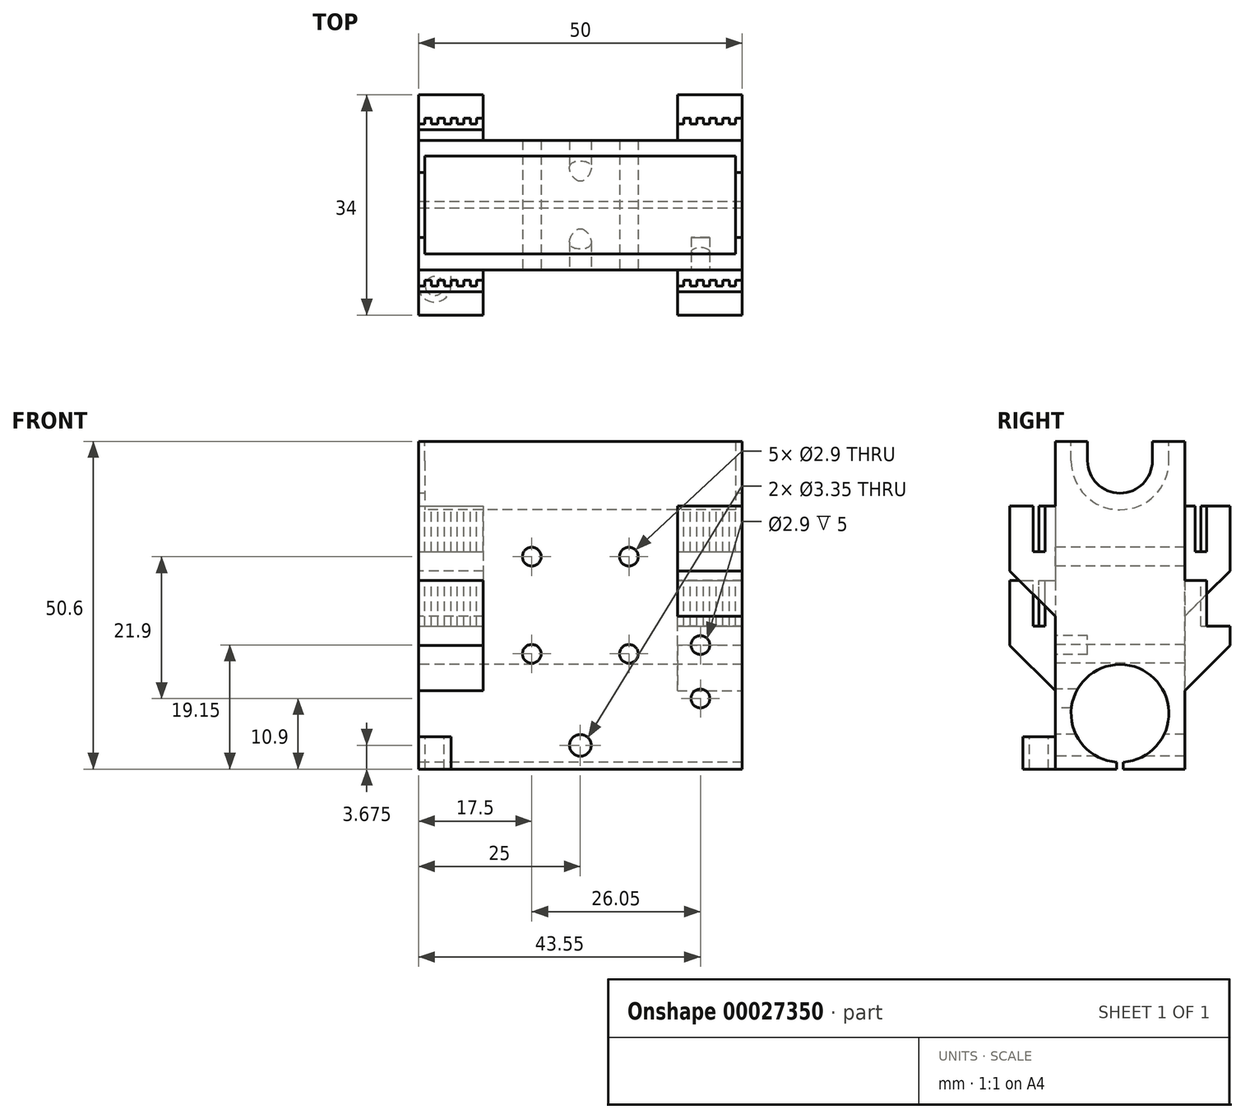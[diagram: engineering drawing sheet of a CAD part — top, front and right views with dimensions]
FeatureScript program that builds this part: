
annotation { "Feature Type Name" : "Feature", "Feature Type Description" : "" }
export const myFeature = defineFeature(function(context is Context, id is Id, definition is map)
    precondition{}
    {
        {
            var Q0;
            Q0=qCreatedBy(makeId("Top.planeOp"),FACE);
            var sketch = newSketch(context, id + "F0", { "sketchPlane" : qUnion([Q0])});
            skLineSegment(sketch, "E0.bottom", {"start": v(0, 0) * mm, "end": v(50, 0) * mm});
            skLineSegment(sketch, "E0.top", {"start": v(0, 20) * mm, "end": v(50, 20) * mm});
            skLineSegment(sketch, "E0.left", {"start": v(0, 0) * mm, "end": v(0, 20) * mm});
            skLineSegment(sketch, "E0.right", {"start": v(50, 0) * mm, "end": v(50, 20) * mm});
            skSolve(sketch);
        }
        {
            var Q0;
            Q0=qSketchRegion(id+"F0",true);
            extrude(context, id + "F1", {"entities" : qUnion([Q0]), "depth" : 50.6 * mm});
        }
        {
            var Q0;
            Q0=makeQuery(id+"F1.opExtrude","SWEPT_FACE",FACE,{"disambiguationData":[OSD([sQuery(id+"F0.wireOp",EDGE,"E0.left")])]});
            var sketch = newSketch(context, id + "F2", { "sketchPlane" : qUnion([Q0])});
            skCircle(sketch, "E1", {"center": v(-10, 8.6) * mm, "radius": 7.55 * mm});
            skCircle(sketch, "E2", {"center": v(-10, 47.6) * mm, "radius": 5 * mm});
            skLineSegment(sketch, "E3", {"start": v(-20, 47.6) * mm, "end": v(0, 47.6) * mm, "construction": true});
            skLineSegment(sketch, "E4", {"start": v(-15, 50.6) * mm, "end": v(-15, 47.6) * mm});
            skLineSegment(sketch, "E5", {"start": v(-5, 50.6) * mm, "end": v(-5, 47.6) * mm});
            skLineSegment(sketch, "E6", {"start": v(-20, 8.6) * mm, "end": v(0, 8.6) * mm, "construction": true});
            skLineSegment(sketch, "E7", {"start": v(-10, 8.6) * mm, "end": v(-10, 0) * mm, "construction": true});
            skLineSegment(sketch, "E8", {"start": v(-10, 0) * mm, "end": v(-10.5, 0) * mm});
            skLineSegment(sketch, "E9", {"start": v(-10.5, 0) * mm, "end": v(-10.5, 1.07) * mm});
            skLineSegment(sketch, "E10", {"start": v(-10.5, 1.07) * mm, "end": v(-9.5, 1.07) * mm});
            skLineSegment(sketch, "E11", {"start": v(-9.5, 1.07) * mm, "end": v(-9.5, 0) * mm});
            skLineSegment(sketch, "E12", {"start": v(-9.5, 0) * mm, "end": v(-10, 0) * mm});
            skLineSegment(sketch, "E13", {"start": v(-10, 15.6) * mm, "end": v(-10, 16.15) * mm});
            skLineSegment(sketch, "E14", {"start": v(-10, 15.6) * mm, "end": v(-5.53, 14.68) * mm});
            skLineSegment(sketch, "E15", {"start": v(-10, 15.6) * mm, "end": v(-14.47, 14.68) * mm});
            skCircle(sketch, "E16", {"center": v(-10, 47.6) * mm, "radius": 7.55 * mm});
            skLineSegment(sketch, "E17", {"start": v(-2.45, 47.6) * mm, "end": v(-2.45, 50.6) * mm});
            skLineSegment(sketch, "E18", {"start": v(-17.55, 47.6) * mm, "end": v(-17.55, 50.6) * mm});
            skSolve(sketch);
        }
        {
            var Q0;
            {var subQ0=sQuery(id+"F2.wireOp",EDGE,"E14");var subQ1=sQuery(id+"F2.wireOp",EDGE,"E1");var subQ3=makeQuery(id+"F2.imprint","INTERSECT",VERTEX,{"disambiguationData":[OD(0.0)],"derivedFrom":[subQ1,subQ0]});Q0=makeQuery(id+"F2.imprint","IMPRINT",FACE,{"disambiguationData":[TD([[makeQuery(id+"F2.imprint","IMPRINT",EDGE,{"disambiguationData":[TD([[subQ3,-1.0]])],"derivedFrom":subQ1}),1.0]])]});}
            var Q1;
            {var subQ0=sQuery(id+"F2.wireOp",EDGE,"E15");var subQ1=sQuery(id+"F2.wireOp",EDGE,"E1");var subQ3=makeQuery(id+"F2.imprint","INTERSECT",VERTEX,{"disambiguationData":[OD(0.0)],"derivedFrom":[subQ1,subQ0]});Q1=makeQuery(id+"F2.imprint","IMPRINT",FACE,{"disambiguationData":[TD([[makeQuery(id+"F2.imprint","IMPRINT",EDGE,{"disambiguationData":[TD([[subQ3,1.0]])],"derivedFrom":subQ1}),1.0]])]});}
            var Q2;
            Q2=makeQuery(id+"F2.imprint","IMPRINT",FACE,{"disambiguationData":[TD([[makeQuery(id+"F2.imprint","IMPRINT",EDGE,{"derivedFrom":sQuery(id+"F2.wireOp",EDGE,"E8")}),-1.0]])]});
            var Q3;
            {var subQ0=sQuery(id+"F2.wireOp",EDGE,"E10");Q3=makeQuery(id+"F2.imprint","IMPRINT",FACE,{"disambiguationData":[TD([[makeQuery(id+"F2.imprint","IMPRINT",EDGE,{"derivedFrom":subQ0}),-1.0]])]});}
            var Q4;
            {var subQ3=sQuery(id+"F2.wireOp",EDGE,"E13");Q4=makeQuery(id+"F2.imprint","IMPRINT",FACE,{"disambiguationData":[TD([[makeQuery(id+"F2.imprint","IMPRINT",EDGE,{"derivedFrom":subQ3}),-1.0]])]});}
            var Q5;
            {var subQ3=sQuery(id+"F2.wireOp",EDGE,"E13");Q5=makeQuery(id+"F2.imprint","IMPRINT",FACE,{"disambiguationData":[TD([[makeQuery(id+"F2.imprint","IMPRINT",EDGE,{"derivedFrom":subQ3}),1.0]])]});}
            var Q6;
            {var subQ7=sQuery(id+"F2.wireOp",EDGE,"E10");Q6=makeQuery(id+"F2.imprint","IMPRINT",FACE,{"disambiguationData":[TD([[makeQuery(id+"F2.imprint","IMPRINT",EDGE,{"derivedFrom":subQ7}),1.0]])]});}
            var Q7;
            {var subQ3=sQuery(id+"F2.wireOp",EDGE,"E5");Q7=makeQuery(id+"F2.imprint","IMPRINT",FACE,{"disambiguationData":[TD([[makeQuery(id+"F2.imprint","IMPRINT",EDGE,{"derivedFrom":subQ3}),-1.0]])]});}
            var Q8;
            {var subQ0=sQuery(id+"F2.wireOp",EDGE,"E4");Q8=makeQuery(id+"F2.imprint","IMPRINT",FACE,{"disambiguationData":[TD([[makeQuery(id+"F2.imprint","IMPRINT",EDGE,{"derivedFrom":subQ0}),1.0]])]});}
            var Q9;
            {var subQ0=sQuery(id+"F2.wireOp",EDGE,"E4");Q9=makeQuery(id+"F2.imprint","IMPRINT",FACE,{"disambiguationData":[TD([[makeQuery(id+"F2.imprint","IMPRINT",EDGE,{"derivedFrom":subQ0}),1.0]])]});}
            var Q10;
            {var subQ3=sQuery(id+"F2.wireOp",EDGE,"E5");Q10=makeQuery(id+"F2.imprint","IMPRINT",FACE,{"disambiguationData":[TD([[makeQuery(id+"F2.imprint","IMPRINT",EDGE,{"derivedFrom":subQ3}),-1.0]])]});}
            var Q11;
            {var subQ1=sQuery(id+"F2.wireOp",EDGE,"E2");var subQ4=makeQuery(id+"F2.imprint","INTERSECT",VERTEX,{"derivedFrom":[subQ1,sQuery(id+"F2.wireOp",EDGE,"E5")]});Q11=makeQuery(id+"F2.imprint","IMPRINT",FACE,{"disambiguationData":[TD([[makeQuery(id+"F2.imprint","IMPRINT",EDGE,{"disambiguationData":[TD([[subQ4,-1.0]])],"derivedFrom":subQ1}),1.0]])]});}
            extrude(context, id + "F3", {"entities" : qUnion([Q0, Q1, Q2, Q3, Q4, Q5, Q6, Q7, Q8, Q9, Q10, Q11]), "operationType" : NewBodyOperationType.REMOVE, "endBound" : BoundingType.THROUGH_ALL, "oppositeDirection" : true, "depth" : 25 * mm});
        }
        {
            var Q0;
            {var subQ3=sQuery(id+"F2.wireOp",EDGE,"E4");Q0=makeQuery(id+"F2.imprint","IMPRINT",FACE,{"disambiguationData":[TD([[makeQuery(id+"F2.imprint","IMPRINT",EDGE,{"derivedFrom":subQ3}),-1.0]])]});}
            var Q1;
            {var subQ3=sQuery(id+"F2.wireOp",EDGE,"E18");Q1=makeQuery(id+"F2.imprint","IMPRINT",FACE,{"disambiguationData":[TD([[makeQuery(id+"F2.imprint","IMPRINT",EDGE,{"derivedFrom":subQ3}),-1.0]])]});}
            var Q2;
            {var subQ3=sQuery(id+"F2.wireOp",EDGE,"E17");Q2=makeQuery(id+"F2.imprint","IMPRINT",FACE,{"disambiguationData":[TD([[makeQuery(id+"F2.imprint","IMPRINT",EDGE,{"derivedFrom":subQ3}),1.0]])]});}
            extrude(context, id + "F4", {"entities" : qUnion([Q0, Q1, Q2]), "operationType" : NewBodyOperationType.REMOVE, "oppositeDirection" : true, "depth" : 49 * mm});
        }
        {
            var Q0;
            {var subQ3=sQuery(id+"F2.wireOp",EDGE,"E4");Q0=makeQuery(id+"F2.imprint","IMPRINT",FACE,{"disambiguationData":[TD([[makeQuery(id+"F2.imprint","IMPRINT",EDGE,{"derivedFrom":subQ3}),-1.0]])]});}
            var Q1;
            {var subQ3=sQuery(id+"F2.wireOp",EDGE,"E18");Q1=makeQuery(id+"F2.imprint","IMPRINT",FACE,{"disambiguationData":[TD([[makeQuery(id+"F2.imprint","IMPRINT",EDGE,{"derivedFrom":subQ3}),-1.0]])]});}
            var Q2;
            {var subQ3=sQuery(id+"F2.wireOp",EDGE,"E17");Q2=makeQuery(id+"F2.imprint","IMPRINT",FACE,{"disambiguationData":[TD([[makeQuery(id+"F2.imprint","IMPRINT",EDGE,{"derivedFrom":subQ3}),1.0]])]});}
            extrude(context, id + "F5", {"entities" : qUnion([Q0, Q1, Q2]), "operationType" : NewBodyOperationType.ADD, "oppositeDirection" : true, "depth" : 16.21 * mm});
        }
        {
            var Q0;
            {var subQ3=sQuery(id+"F2.wireOp",EDGE,"E4");Q0=makeQuery(id+"F2.imprint","IMPRINT",FACE,{"disambiguationData":[TD([[makeQuery(id+"F2.imprint","IMPRINT",EDGE,{"derivedFrom":subQ3}),-1.0]])]});}
            var Q1;
            {var subQ3=sQuery(id+"F2.wireOp",EDGE,"E18");Q1=makeQuery(id+"F2.imprint","IMPRINT",FACE,{"disambiguationData":[TD([[makeQuery(id+"F2.imprint","IMPRINT",EDGE,{"derivedFrom":subQ3}),-1.0]])]});}
            var Q2;
            {var subQ3=sQuery(id+"F2.wireOp",EDGE,"E17");Q2=makeQuery(id+"F2.imprint","IMPRINT",FACE,{"disambiguationData":[TD([[makeQuery(id+"F2.imprint","IMPRINT",EDGE,{"derivedFrom":subQ3}),1.0]])]});}
            extrude(context, id + "F6", {"entities" : qUnion([Q0, Q1, Q2]), "operationType" : NewBodyOperationType.REMOVE, "oppositeDirection" : true, "depth" : 23.25 * mm});
        }
        {
            var Q0;
            {var subQ3=sQuery(id+"F2.wireOp",EDGE,"E4");Q0=makeQuery(id+"F2.imprint","IMPRINT",FACE,{"disambiguationData":[TD([[makeQuery(id+"F2.imprint","IMPRINT",EDGE,{"derivedFrom":subQ3}),-1.0]])]});}
            var Q1;
            {var subQ3=sQuery(id+"F2.wireOp",EDGE,"E18");Q1=makeQuery(id+"F2.imprint","IMPRINT",FACE,{"disambiguationData":[TD([[makeQuery(id+"F2.imprint","IMPRINT",EDGE,{"derivedFrom":subQ3}),-1.0]])]});}
            var Q2;
            {var subQ3=sQuery(id+"F2.wireOp",EDGE,"E17");Q2=makeQuery(id+"F2.imprint","IMPRINT",FACE,{"disambiguationData":[TD([[makeQuery(id+"F2.imprint","IMPRINT",EDGE,{"derivedFrom":subQ3}),1.0]])]});}
            extrude(context, id + "F7", {"entities" : qUnion([Q0, Q1, Q2]), "operationType" : NewBodyOperationType.ADD, "oppositeDirection" : true, "depth" : 1 * mm});
        }
        {
            var Q0;
            Q0=makeQuery(id+"F1.opExtrude","SWEPT_FACE",FACE,{"disambiguationData":[OSD([sQuery(id+"F0.wireOp",EDGE,"E0.bottom")])]});
            var sketch = newSketch(context, id + "F8", { "sketchPlane" : qUnion([Q0])});
            skLineSegment(sketch, "E19.bottom", {"start": v(0, 29.1) * mm, "end": v(10, 29.1) * mm});
            skLineSegment(sketch, "E19.top", {"start": v(0, 9.1) * mm, "end": v(10, 9.1) * mm});
            skLineSegment(sketch, "E19.left", {"start": v(0, 29.1) * mm, "end": v(0, 9.1) * mm});
            skLineSegment(sketch, "E19.right", {"start": v(10, 29.1) * mm, "end": v(10, 9.1) * mm});
            skLineSegment(sketch, "E20.bottom", {"start": v(50, 40.6) * mm, "end": v(40, 40.6) * mm});
            skLineSegment(sketch, "E20.top", {"start": v(50, 20.6) * mm, "end": v(40, 20.6) * mm});
            skLineSegment(sketch, "E20.left", {"start": v(50, 40.6) * mm, "end": v(50, 20.6) * mm});
            skLineSegment(sketch, "E20.right", {"start": v(40, 40.6) * mm, "end": v(40, 20.6) * mm});
            skPoint(sketch, "E21", {"position": v(0, 47.6) * mm});
            skPoint(sketch, "E22", {"position": v(0, 8.6) * mm});
            skSolve(sketch);
        }
        {
            var Q0;
            Q0=qSketchRegion(id+"F8",true);
            extrude(context, id + "F9", {"entities" : qUnion([Q0]), "operationType" : NewBodyOperationType.ADD, "depth" : 7 * mm});
        }
        {
            var Q0;
            Q0=makeQuery(id+"F9.opExtrude","CAP_EDGE",EDGE,{"disambiguationData":[OSD([sQuery(id+"F8.wireOp",EDGE,"E19.top")])],"isStart":false});
            var Q1;
            Q1=makeQuery(id+"F9.opExtrude","CAP_EDGE",EDGE,{"disambiguationData":[OSD([sQuery(id+"F8.wireOp",EDGE,"E20.top")])],"isStart":false});
            chamfer(context, id + "F10", {"entities" : qUnion([Q0, Q1]), "width" : 10 * mm, "tangentPropagation" : true});
        }
        {
            var Q0;
            Q0=makeQuery(id+"F9.opExtrude","SWEPT_FACE",FACE,{"disambiguationData":[OSD([sQuery(id+"F8.wireOp",EDGE,"E19.bottom")])]});
            var sketch = newSketch(context, id + "F11", { "sketchPlane" : qUnion([Q0])});
            skLineSegment(sketch, "E23", {"start": v(-935.9, 0) * mm, "end": v(-935.88, -4.54) * mm});
            skLineSegment(sketch, "E24.left", {"start": v(0, -3.4) * mm, "end": v(0, -1.6) * mm});
            skLineSegment(sketch, "E25", {"start": v(6, -2.5) * mm, "end": v(7, -2.5) * mm});
            skLineSegment(sketch, "E26", {"start": v(4, -2.5) * mm, "end": v(5, -2.5) * mm});
            skLineSegment(sketch, "E27", {"start": v(0, -2.5) * mm, "end": v(1, -2.5) * mm});
            skLineSegment(sketch, "E28", {"start": v(7, -1.6) * mm, "end": v(8, -1.6) * mm});
            skLineSegment(sketch, "E29", {"start": v(2, -2.5) * mm, "end": v(3, -2.5) * mm});
            skLineSegment(sketch, "E30", {"start": v(3, -1.6) * mm, "end": v(4, -1.6) * mm});
            skLineSegment(sketch, "E31", {"start": v(8, -2.5) * mm, "end": v(9, -2.5) * mm});
            skLineSegment(sketch, "E32", {"start": v(8, -1.6) * mm, "end": v(8, -2.5) * mm});
            skLineSegment(sketch, "E33", {"start": v(9, -2.5) * mm, "end": v(9, -1.6) * mm});
            skLineSegment(sketch, "E34", {"start": v(10, -1.6) * mm, "end": v(10, -2.5) * mm});
            skLineSegment(sketch, "E35", {"start": v(6, -1.6) * mm, "end": v(6, -2.5) * mm});
            skLineSegment(sketch, "E36", {"start": v(2, -1.6) * mm, "end": v(2, -2.5) * mm});
            skLineSegment(sketch, "E37", {"start": v(1, -1.6) * mm, "end": v(2, -1.6) * mm});
            skLineSegment(sketch, "E38", {"start": v(1, -2.5) * mm, "end": v(1, -1.6) * mm});
            skLineSegment(sketch, "E39", {"start": v(9, -1.6) * mm, "end": v(10, -1.6) * mm});
            skLineSegment(sketch, "E40", {"start": v(5, -1.6) * mm, "end": v(6, -1.6) * mm});
            skLineSegment(sketch, "E41", {"start": v(5, -2.5) * mm, "end": v(5, -1.6) * mm});
            skLineSegment(sketch, "E42", {"start": v(3, -2.5) * mm, "end": v(3, -1.6) * mm});
            skLineSegment(sketch, "E43", {"start": v(4, -1.6) * mm, "end": v(4, -2.5) * mm});
            skLineSegment(sketch, "E44", {"start": v(7, -2.5) * mm, "end": v(7, -1.6) * mm});
            skLineSegment(sketch, "E45", {"start": v(0, -1.6) * mm, "end": v(0, -2.5) * mm});
            skLineSegment(sketch, "E46", {"start": v(10, -2.5) * mm, "end": v(10, -3.4) * mm});
            skLineSegment(sketch, "E47", {"start": v(0, -3.4) * mm, "end": v(10, -3.4) * mm});
            skLineSegment(sketch, "E48", {"start": v(5.3, -1.6) * mm, "end": v(5.3, 0) * mm});
            skSolve(sketch);
        }
        {
            var Q0;
            Q0=qSketchRegion(id+"F11",true);
            extrude(context, id + "F12", {"entities" : qUnion([Q0]), "operationType" : NewBodyOperationType.REMOVE, "oppositeDirection" : true, "depth" : 7 * mm});
        }
        {
            var Q0;
            Q0=makeQuery(id+"F9.opExtrude","SWEPT_FACE",FACE,{"disambiguationData":[OSD([sQuery(id+"F8.wireOp",EDGE,"E20.bottom")])]});
            var sketch = newSketch(context, id + "F13", { "sketchPlane" : qUnion([Q0])});
            skLineSegment(sketch, "E49.left", {"start": v(40, -3.4) * mm, "end": v(40, -1.6) * mm});
            skLineSegment(sketch, "E50", {"start": v(46, -2.5) * mm, "end": v(47, -2.5) * mm});
            skLineSegment(sketch, "E51", {"start": v(44, -2.5) * mm, "end": v(45, -2.5) * mm});
            skLineSegment(sketch, "E52", {"start": v(40, -2.5) * mm, "end": v(41, -2.5) * mm});
            skLineSegment(sketch, "E53", {"start": v(47, -1.6) * mm, "end": v(48, -1.6) * mm});
            skLineSegment(sketch, "E54", {"start": v(42, -2.5) * mm, "end": v(43, -2.5) * mm});
            skLineSegment(sketch, "E55", {"start": v(43, -1.6) * mm, "end": v(44, -1.6) * mm});
            skLineSegment(sketch, "E56", {"start": v(48, -2.5) * mm, "end": v(49, -2.5) * mm});
            skLineSegment(sketch, "E57", {"start": v(48, -1.6) * mm, "end": v(48, -2.5) * mm});
            skLineSegment(sketch, "E58", {"start": v(49, -2.5) * mm, "end": v(49, -1.6) * mm});
            skLineSegment(sketch, "E59", {"start": v(50, -1.6) * mm, "end": v(50, -2.5) * mm});
            skLineSegment(sketch, "E60", {"start": v(46, -1.6) * mm, "end": v(46, -2.5) * mm});
            skLineSegment(sketch, "E61", {"start": v(42, -1.6) * mm, "end": v(42, -2.5) * mm});
            skLineSegment(sketch, "E62", {"start": v(41, -1.6) * mm, "end": v(42, -1.6) * mm});
            skLineSegment(sketch, "E63", {"start": v(41, -2.5) * mm, "end": v(41, -1.6) * mm});
            skLineSegment(sketch, "E64", {"start": v(49, -1.6) * mm, "end": v(50, -1.6) * mm});
            skLineSegment(sketch, "E65", {"start": v(45, -1.6) * mm, "end": v(46, -1.6) * mm});
            skLineSegment(sketch, "E66", {"start": v(45, -2.5) * mm, "end": v(45, -1.6) * mm});
            skLineSegment(sketch, "E67", {"start": v(43, -2.5) * mm, "end": v(43, -1.6) * mm});
            skLineSegment(sketch, "E68", {"start": v(44, -1.6) * mm, "end": v(44, -2.5) * mm});
            skLineSegment(sketch, "E69", {"start": v(47, -2.5) * mm, "end": v(47, -1.6) * mm});
            skLineSegment(sketch, "E70", {"start": v(40, -1.6) * mm, "end": v(40, -2.5) * mm});
            skLineSegment(sketch, "E71", {"start": v(50, -2.5) * mm, "end": v(50, -3.4) * mm});
            skLineSegment(sketch, "E72", {"start": v(40, -3.4) * mm, "end": v(50, -3.4) * mm});
            skLineSegment(sketch, "E73", {"start": v(45.23, -1.6) * mm, "end": v(45.23, 0) * mm});
            skSolve(sketch);
        }
        {
            var Q0;
            Q0=qSketchRegion(id+"F13",true);
            extrude(context, id + "F14", {"entities" : qUnion([Q0]), "operationType" : NewBodyOperationType.REMOVE, "oppositeDirection" : true, "depth" : 7 * mm});
        }
        {
            var Q0;
            Q0=makeQuery(id+"F1.opExtrude","SWEPT_FACE",FACE,{"disambiguationData":[OSD([sQuery(id+"F0.wireOp",EDGE,"E0.top")])]});
            var sketch = newSketch(context, id + "F15", { "sketchPlane" : qUnion([Q0])});
            skLineSegment(sketch, "E74.bottom", {"start": v(-50, 9.1) * mm, "end": v(-40, 9.1) * mm});
            skLineSegment(sketch, "E74.top", {"start": v(-50, 29.1) * mm, "end": v(-40, 29.1) * mm});
            skLineSegment(sketch, "E74.left", {"start": v(-50, 9.1) * mm, "end": v(-50, 29.1) * mm});
            skLineSegment(sketch, "E74.right", {"start": v(-40, 9.1) * mm, "end": v(-40, 29.1) * mm});
            skLineSegment(sketch, "E75.bottom", {"start": v(0, 40.6) * mm, "end": v(-10, 40.6) * mm});
            skLineSegment(sketch, "E75.top", {"start": v(0, 20.6) * mm, "end": v(-10, 20.6) * mm});
            skLineSegment(sketch, "E75.left", {"start": v(0, 40.6) * mm, "end": v(0, 20.6) * mm});
            skLineSegment(sketch, "E75.right", {"start": v(-10, 40.6) * mm, "end": v(-10, 20.6) * mm});
            skSolve(sketch);
        }
        {
            var Q0;
            Q0=qSketchRegion(id+"F15",true);
            extrude(context, id + "F16", {"entities" : qUnion([Q0]), "operationType" : NewBodyOperationType.ADD, "depth" : 7 * mm});
        }
        {
            var Q0;
            Q0=makeQuery(id+"F16.opExtrude","SWEPT_FACE",FACE,{"disambiguationData":[OSD([sQuery(id+"F15.wireOp",EDGE,"E74.top")])]});
            var sketch = newSketch(context, id + "F17", { "sketchPlane" : qUnion([Q0])});
            skLineSegment(sketch, "E76.left", {"start": v(40, 21.6) * mm, "end": v(40, 23.4) * mm});
            skLineSegment(sketch, "E77", {"start": v(46, 22.5) * mm, "end": v(47, 22.5) * mm});
            skLineSegment(sketch, "E78", {"start": v(44, 22.5) * mm, "end": v(45, 22.5) * mm});
            skLineSegment(sketch, "E79", {"start": v(40, 22.5) * mm, "end": v(41, 22.5) * mm});
            skLineSegment(sketch, "E80", {"start": v(47, 23.4) * mm, "end": v(48, 23.4) * mm});
            skLineSegment(sketch, "E81", {"start": v(42, 22.5) * mm, "end": v(43, 22.5) * mm});
            skLineSegment(sketch, "E82", {"start": v(43, 23.4) * mm, "end": v(44, 23.4) * mm});
            skLineSegment(sketch, "E83", {"start": v(48, 22.5) * mm, "end": v(49, 22.5) * mm});
            skLineSegment(sketch, "E84", {"start": v(48, 23.4) * mm, "end": v(48, 22.5) * mm});
            skLineSegment(sketch, "E85", {"start": v(49, 22.5) * mm, "end": v(49, 23.4) * mm});
            skLineSegment(sketch, "E86", {"start": v(50, 23.4) * mm, "end": v(50, 22.5) * mm});
            skLineSegment(sketch, "E87", {"start": v(46, 23.4) * mm, "end": v(46, 22.5) * mm});
            skLineSegment(sketch, "E88", {"start": v(42, 23.4) * mm, "end": v(42, 22.5) * mm});
            skLineSegment(sketch, "E89", {"start": v(41, 23.4) * mm, "end": v(42, 23.4) * mm});
            skLineSegment(sketch, "E90", {"start": v(41, 22.5) * mm, "end": v(41, 23.4) * mm});
            skLineSegment(sketch, "E91", {"start": v(49, 23.4) * mm, "end": v(50, 23.4) * mm});
            skLineSegment(sketch, "E92", {"start": v(45, 23.4) * mm, "end": v(46, 23.4) * mm});
            skLineSegment(sketch, "E93", {"start": v(45, 22.5) * mm, "end": v(45, 23.4) * mm});
            skLineSegment(sketch, "E94", {"start": v(43, 22.5) * mm, "end": v(43, 23.4) * mm});
            skLineSegment(sketch, "E95", {"start": v(44, 23.4) * mm, "end": v(44, 22.5) * mm});
            skLineSegment(sketch, "E96", {"start": v(47, 22.5) * mm, "end": v(47, 23.4) * mm});
            skLineSegment(sketch, "E97", {"start": v(40, 23.4) * mm, "end": v(40, 22.5) * mm});
            skLineSegment(sketch, "E98", {"start": v(50, 22.5) * mm, "end": v(50, 21.6) * mm});
            skLineSegment(sketch, "E99", {"start": v(40, 21.6) * mm, "end": v(50, 21.6) * mm});
            skLineSegment(sketch, "E100", {"start": v(45, 21.6) * mm, "end": v(45, 20) * mm});
            skSolve(sketch);
        }
        {
            var Q0;
            {var subQ4=sQuery(id+"F17.wireOp",EDGE,"E76.left");Q0=makeQuery(id+"F17.imprint","IMPRINT",FACE,{"disambiguationData":[TD([[makeQuery(id+"F17.imprint","IMPRINT",EDGE,{"derivedFrom":subQ4}),1.0]])]});}
            extrude(context, id + "F18", {"entities" : qUnion([Q0]), "operationType" : NewBodyOperationType.REMOVE, "oppositeDirection" : true, "depth" : 7 * mm});
        }
        {
            var Q0;
            Q0=makeQuery(id+"F16.opExtrude","SWEPT_FACE",FACE,{"disambiguationData":[OSD([sQuery(id+"F15.wireOp",EDGE,"E75.bottom")])]});
            var sketch = newSketch(context, id + "F19", { "sketchPlane" : qUnion([Q0])});
            skLineSegment(sketch, "E101", {"start": v(6, 22.5) * mm, "end": v(7, 22.5) * mm});
            skLineSegment(sketch, "E102", {"start": v(4, 22.5) * mm, "end": v(5, 22.5) * mm});
            skLineSegment(sketch, "E103", {"start": v(0, 22.5) * mm, "end": v(1, 22.5) * mm});
            skLineSegment(sketch, "E104", {"start": v(7, 23.4) * mm, "end": v(8, 23.4) * mm});
            skLineSegment(sketch, "E105", {"start": v(2, 22.5) * mm, "end": v(3, 22.5) * mm});
            skLineSegment(sketch, "E106", {"start": v(3, 23.4) * mm, "end": v(4, 23.4) * mm});
            skLineSegment(sketch, "E107", {"start": v(8, 22.5) * mm, "end": v(9, 22.5) * mm});
            skLineSegment(sketch, "E108", {"start": v(8, 23.4) * mm, "end": v(8, 22.5) * mm});
            skLineSegment(sketch, "E109", {"start": v(9, 22.5) * mm, "end": v(9, 23.4) * mm});
            skLineSegment(sketch, "E110", {"start": v(10, 23.4) * mm, "end": v(10, 22.5) * mm});
            skLineSegment(sketch, "E111", {"start": v(6, 23.4) * mm, "end": v(6, 22.5) * mm});
            skLineSegment(sketch, "E112", {"start": v(2, 23.4) * mm, "end": v(2, 22.5) * mm});
            skLineSegment(sketch, "E113", {"start": v(1, 23.4) * mm, "end": v(2, 23.4) * mm});
            skLineSegment(sketch, "E114", {"start": v(1, 22.5) * mm, "end": v(1, 23.4) * mm});
            skLineSegment(sketch, "E115", {"start": v(9, 23.4) * mm, "end": v(10, 23.4) * mm});
            skLineSegment(sketch, "E116", {"start": v(5, 23.4) * mm, "end": v(6, 23.4) * mm});
            skLineSegment(sketch, "E117", {"start": v(5, 22.5) * mm, "end": v(5, 23.4) * mm});
            skLineSegment(sketch, "E118", {"start": v(3, 22.5) * mm, "end": v(3, 23.4) * mm});
            skLineSegment(sketch, "E119", {"start": v(4, 23.4) * mm, "end": v(4, 22.5) * mm});
            skLineSegment(sketch, "E120", {"start": v(7, 22.5) * mm, "end": v(7, 23.4) * mm});
            skLineSegment(sketch, "E121", {"start": v(10, 22.5) * mm, "end": v(10, 21.6) * mm});
            skLineSegment(sketch, "E122", {"start": v(0, 21.6) * mm, "end": v(10, 21.6) * mm});
            skLineSegment(sketch, "E123", {"start": v(5, 21.6) * mm, "end": v(5, 20) * mm});
            skLineSegment(sketch, "E124", {"start": v(0, 21.6) * mm, "end": v(0, 22.5) * mm});
            skSolve(sketch);
        }
        {
            var Q0;
            Q0=makeQuery(id+"F19.imprint","IMPRINT",FACE,{"disambiguationData":[TD([[makeQuery(id+"F19.imprint","IMPRINT",EDGE,{"derivedFrom":sQuery(id+"F19.wireOp",EDGE,"E101")}),-1.0]])]});
            extrude(context, id + "F20", {"entities" : qUnion([Q0]), "operationType" : NewBodyOperationType.REMOVE, "oppositeDirection" : true, "depth" : 7 * mm});
        }
        {
            var Q0;
            Q0=makeQuery(id+"F16.opExtrude","CAP_EDGE",EDGE,{"disambiguationData":[OSD([sQuery(id+"F15.wireOp",EDGE,"E75.top")])],"isStart":false});
            var Q1;
            Q1=makeQuery(id+"F16.opExtrude","CAP_EDGE",EDGE,{"disambiguationData":[OSD([sQuery(id+"F15.wireOp",EDGE,"E74.bottom")])],"isStart":false});
            chamfer(context, id + "F21", {"entities" : qUnion([Q0, Q1]), "width" : 10 * mm, "tangentPropagation" : true});
        }
        {
            var Q0;
            Q0=makeQuery(id+"F1.opExtrude","SWEPT_FACE",FACE,{"disambiguationData":[OSD([sQuery(id+"F0.wireOp",EDGE,"E0.bottom")])]});
            var sketch = newSketch(context, id + "F22", { "sketchPlane" : qUnion([Q0])});
            skCircle(sketch, "E125", {"center": v(17.5, 32.8) * mm, "radius": 1.45 * mm});
            skCircle(sketch, "E126", {"center": v(32.5, 32.8) * mm, "radius": 1.45 * mm});
            skCircle(sketch, "E127", {"center": v(17.5, 17.8) * mm, "radius": 1.45 * mm});
            skCircle(sketch, "E128", {"center": v(32.5, 17.8) * mm, "radius": 1.45 * mm});
            skLineSegment(sketch, "E129", {"start": v(17.5, 32.8) * mm, "end": v(0, 32.8) * mm});
            skLineSegment(sketch, "E130", {"start": v(32.5, 17.8) * mm, "end": v(50, 17.8) * mm});
            skLineSegment(sketch, "E131", {"start": v(32.5, 32.8) * mm, "end": v(32.5, 50.6) * mm});
            skLineSegment(sketch, "E132", {"start": v(17.5, 17.8) * mm, "end": v(17.5, 0) * mm});
            skCircle(sketch, "E133", {"center": v(25, 3.68) * mm, "radius": 1.68 * mm});
            skLineSegment(sketch, "E134", {"start": v(25, 0) * mm, "end": v(25, 13.82) * mm, "construction": true});
            skSolve(sketch);
        }
        {
            var Q0;
            Q0=qSketchRegion(id+"F22",true);
            var Q1;
            Q1=makeQuery(id+"F22.imprint","IMPRINT",FACE,{"disambiguationData":[TD([[makeQuery(id+"F22.imprint","IMPRINT",EDGE,{"derivedFrom":sQuery(id+"F22.wireOp",EDGE,"E125")}),1.0]])]});
            var Q2;
            Q2=makeQuery(id+"F22.imprint","IMPRINT",FACE,{"disambiguationData":[TD([[makeQuery(id+"F22.imprint","IMPRINT",EDGE,{"derivedFrom":sQuery(id+"F22.wireOp",EDGE,"E126")}),1.0]])]});
            var Q3;
            Q3=makeQuery(id+"F22.imprint","IMPRINT",FACE,{"disambiguationData":[TD([[makeQuery(id+"F22.imprint","IMPRINT",EDGE,{"derivedFrom":sQuery(id+"F22.wireOp",EDGE,"E128")}),1.0]])]});
            var Q4;
            Q4=makeQuery(id+"F22.imprint","IMPRINT",FACE,{"disambiguationData":[TD([[makeQuery(id+"F22.imprint","IMPRINT",EDGE,{"derivedFrom":sQuery(id+"F22.wireOp",EDGE,"E127")}),1.0]])]});
            extrude(context, id + "F23", {"entities" : qUnion([Q0, Q1, Q2, Q3, Q4]), "operationType" : NewBodyOperationType.REMOVE, "endBound" : BoundingType.THROUGH_ALL, "oppositeDirection" : true, "depth" : 25 * mm});
        }
        {
            var Q0;
            Q0=makeQuery(id+"F1.opExtrude","SWEPT_FACE",FACE,{"disambiguationData":[OSD([sQuery(id+"F0.wireOp",EDGE,"E0.bottom")])]});
            var sketch = newSketch(context, id + "F24", { "sketchPlane" : qUnion([Q0])});
            skCircle(sketch, "E135", {"center": v(43.55, 19.15) * mm, "radius": 1.45 * mm});
            skCircle(sketch, "E136", {"center": v(43.55, 10.9) * mm, "radius": 1.45 * mm});
            skSolve(sketch);
        }
        {
            var Q0;
            Q0=qSketchRegion(id+"F24",true);
            extrude(context, id + "F25", {"entities" : qUnion([Q0]), "operationType" : NewBodyOperationType.REMOVE, "oppositeDirection" : true, "depth" : 5 * mm});
        }
        {
            var Q0;
            Q0=makeQuery(id+"F1.opExtrude","SWEPT_FACE",FACE,{"disambiguationData":[OSD([sQuery(id+"F0.wireOp",EDGE,"E0.bottom")])]});
            var sketch = newSketch(context, id + "F26", { "sketchPlane" : qUnion([Q0])});
            skLineSegment(sketch, "E137.bottom", {"start": v(0, 0) * mm, "end": v(5, 0) * mm});
            skLineSegment(sketch, "E137.top", {"start": v(0, 5) * mm, "end": v(5, 5) * mm});
            skLineSegment(sketch, "E137.left", {"start": v(0, 0) * mm, "end": v(0, 5) * mm});
            skLineSegment(sketch, "E137.right", {"start": v(5, 0) * mm, "end": v(5, 5) * mm});
            skSolve(sketch);
        }
        {
            var Q0;
            Q0=qSketchRegion(id+"F26",true);
            extrude(context, id + "F27", {"entities" : qUnion([Q0]), "operationType" : NewBodyOperationType.ADD, "depth" : 5 * mm});
        }
        {
            var Q0;
            Q0=makeQuery(id+"F27.opExtrude","SWEPT_FACE",FACE,{"disambiguationData":[OSD([sQuery(id+"F26.wireOp",EDGE,"E137.top")])]});
            var sketch = newSketch(context, id + "F28", { "sketchPlane" : qUnion([Q0])});
            skCircle(sketch, "E138", {"center": v(2.5, -2.5) * mm, "radius": 1.45 * mm});
            skLineSegment(sketch, "E139", {"start": v(0, -2.5) * mm, "end": v(5, -2.5) * mm});
            skSolve(sketch);
        }
        {
            var Q0;
            Q0=qSketchRegion(id+"F28",true);
            extrude(context, id + "F29", {"entities" : qUnion([Q0]), "operationType" : NewBodyOperationType.REMOVE, "oppositeDirection" : true, "depth" : 25 * mm});
        }
        {
            var Q0;
            Q0=makeQuery(id+"F27.opExtrude","CAP_EDGE",EDGE,{"disambiguationData":[OSD([sQuery(id+"F26.wireOp",EDGE,"E137.left")])],"isStart":false});
            var Q1;
            Q1=makeQuery(id+"F27.opExtrude","CAP_EDGE",EDGE,{"disambiguationData":[OSD([sQuery(id+"F26.wireOp",EDGE,"E137.right")])],"isStart":false});
            fillet(context, id + "F30", {"entities" : qUnion([Q0, Q1]), "radius" : 2.5 * mm, "tangentPropagation" : true, "allowEdgeOverflow" : false});
        }
    });
